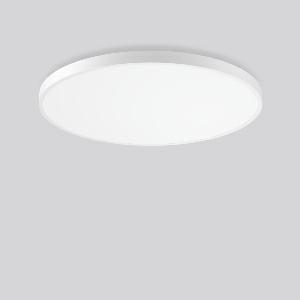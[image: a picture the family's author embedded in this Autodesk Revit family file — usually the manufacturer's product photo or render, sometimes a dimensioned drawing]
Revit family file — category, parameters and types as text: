
# Revit family: triona_round_a_312391_002_1_76_d607
name_source: partatom
category: Lighting Fixtures
units: mm (PartAtom-declared; Revit-internal decimal feet)

## family parameters
Cut with Voids When Loaded = No
Host = Face
Light Source = No
Part Type = Normal
Room Calculation Point = No
Round Connector Dimension = Use Diameter
Shared = No

## types (1)
- TRIONA round A (1 x LED Modul 840, 11700 lm, 4000)
    Apparent Load = 106 VA
    CIE Flux Codes = 49 80 96 100 100
    Color Rendering = 80
    Color Temperature = 4000
    Default Elevation = 1800 mm
    Description = Series: TRIONA round
Decorative round LED surface-mounted luminaire. Flat, seamless frame: aluminium extrusion profile, powder coated. Cover made of sheet steel, powder-coated. Light emission through a diffuser: plastic, opal. Lightguide and diffuser made of non-yellowing plastic (PMMA). Lateral light emission (RZB SIDELITE technology) for above-average homogeneous light distribution. Suitable for Ceiling mounting, Wall (surface). Tool-free mounting via bayonet connection. Electronic ballast included. Very easy installation thanks to Plug+Play connection. 
Colour: traffic white, matt (RAL 9016)
Diameter: 1009 mm
Height: 88 mm
Lamp: LED
Socket: without socket
Colour temperature: 4000K
Colour rendering index (CRI): 80
System power: 106 W
Rated luminous flux: 11700 lm
Luminous efficiency: 110 lm/W
Control gear: Converter, dimmable, DALI
Protection class: I
Type of protection: IP 20
    Height = 88 mm
    Lamp = 1 x LED Modul 840
    Lamp Light Flux = 11700 lm
    Lamp count = 1
    Length = 1009 mm
    Lifetime = 50000 h
    Luminous efficacy = 110 lm/W
    Manufacturer = RZB
    ModVariant = No
    Model = 312391.002.1.76
    Mounting Place = Ceiling
    Mounting Type = Surface mounted
    Number of Poles = 1
    OnlyDefault = Yes
    Power Factor = 1
    Product Name = TRIONA round A
    Product group = Surface mounted modular luminaires
    ProductGroupID = 306
    Protection Class = Protection class I
    Protection Degree = IP 20
    RLX_Detail_Level = 1
    RLX_Emergency_Light_Flux = 0 lm
    RLX_Emergency_Type = 0
    RLX_Emergency_Type_DB = No
    RlxData = <blob elided: 35829 chars, md5=e22f64e7>
    Socket = socket
    Standby Power = 0 W
    System Light Flux = 11700 lm
    System Power = 106 W
    Type Comments = Product without accessories
    Type Image = 312392.002.jpg
    URL = http://relux.com
    VarID = ---
    Voltage = 230 V
    Voltage Range = 220-240 V
    Weight = 0.00 kg
    Width = 0 mm  [stored 0 ft]

note: [stored X ft] marks values corroborated as IEEE doubles in the binary element streams (Revit-internal decimal feet)

## geometry (parser evidence)
native form markers: Blend x4, Sweep x11
no freeform markers — native parametric forms only
